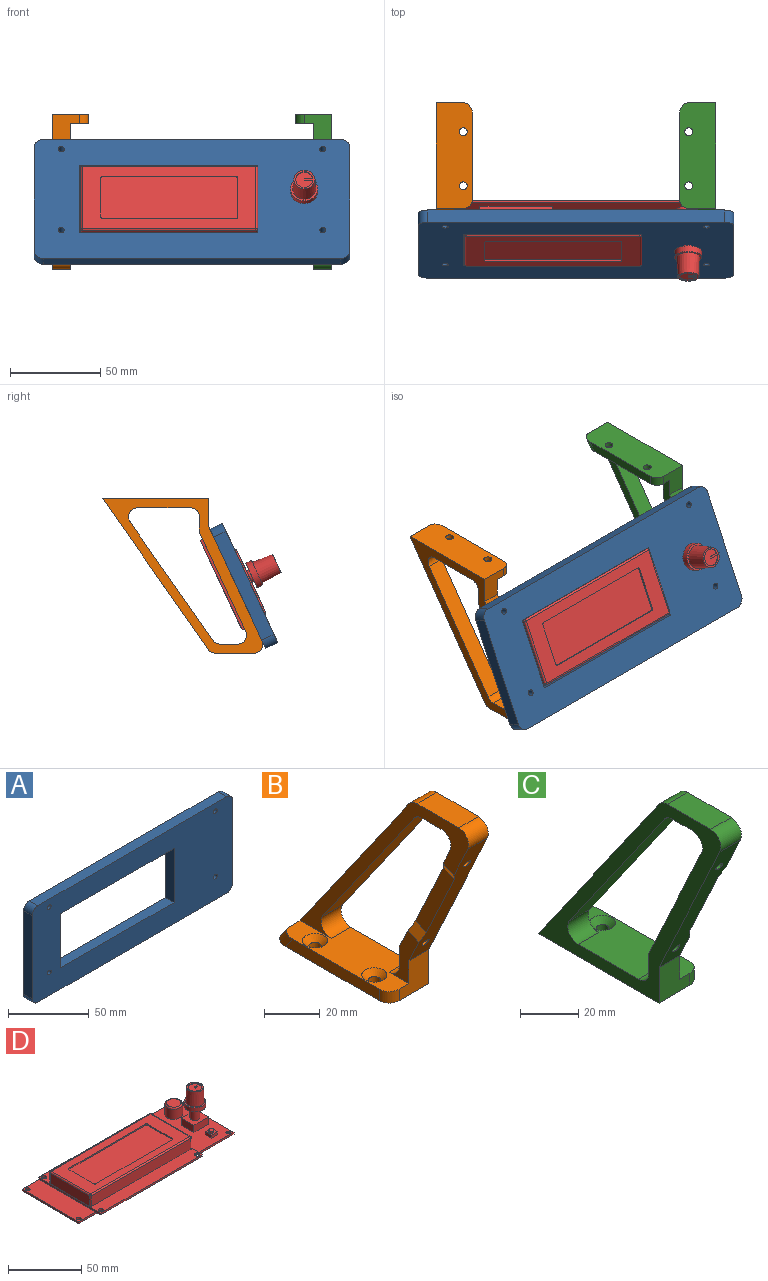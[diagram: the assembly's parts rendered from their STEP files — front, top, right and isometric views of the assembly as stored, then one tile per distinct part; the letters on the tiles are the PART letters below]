
ASSEMBLY  parts=4 mates=3
PART A: 18 faces, bbox 175x7.5x73 mm
  f0: plane 63x7.5mm, normal (1,0,0), area 472.5mm2, adj f8,f9,f10,f13
  f1: plane 165x7.5mm, normal (0,0,1), area 1237.5mm2, adj f8,f9,f10,f11
  f2: plane 63x7.5mm, normal (-1,0,0), area 472.5mm2, adj f8,f9,f11,f12
  f3: plane 99x7.5mm, normal (0,0,1), area 742.5mm2, adj f4,f6,f8,f9
  f4: plane 41x7.5mm, normal (1,0,0), area 307.5mm2, adj f3,f5,f8,f9
  f5: plane 99x7.5mm, normal (0,0,-1), area 742.5mm2, adj f4,f6,f8,f9
  f6: plane 41x7.5mm, normal (-1,0,0), area 307.5mm2, adj f3,f5,f8,f9
  f7: plane 165x7.5mm, normal (0,0,-1), area 1237.5mm2, adj f8,f9,f12,f13
  f8: plane 175x73mm, normal (0,-1,0), area 8660.3mm2, adj f0,f1,f2,f3,f4,f5,f6,f7
  f9: plane 175x73mm, normal (0,1,0), area 8660.3mm2, adj f0,f1,f2,f3,f4,f5,f6,f7
  f10: cylinder r=5mm len=7.5mm, axis (0,1,0), area 58.9mm2, adj f0,f1,f8,f9
  f11: cylinder r=5mm len=7.5mm, axis (0,-1,0), area 58.9mm2, adj f1,f2,f8,f9
  f12: cylinder r=5mm len=7.5mm, axis (0,1,0), area 58.9mm2, adj f2,f7,f8,f9
  f13: cylinder r=5mm len=7.5mm, axis (0,-1,0), area 58.9mm2, adj f0,f7,f8,f9
  f14: cylinder r=1.65mm len=7.5mm, axis (0,1,0), area 77.8mm2, adj f8,f9
  f15: cylinder r=1.65mm len=7.5mm, axis (0,1,0), area 77.8mm2, adj f8,f9
  f16: cylinder r=1.65mm len=7.5mm, axis (0,1,0), area 77.8mm2, adj f8,f9
  f17: cylinder r=1.65mm len=7.5mm, axis (0,1,0), area 77.8mm2, adj f8,f9
PART B: 31 faces, bbox 20x88.7x88.6 mm
  f0: plane 23.15x14.95mm, normal (-1,0,0), area 131.2mm2, adj f1,f4,f5,f9,f10,f22,f24
  f1: plane 55.1x25.7mm, normal (0,0.91,0.42), area 515.3mm2, adj f0,f5,f11,f12,f17,f18,f23,f24
  f2: plane 10x9.55mm, normal (0,0,-1), area 95.5mm2, adj f11,f12,f20,f23
  f3: plane 65.69x46mm, normal (0,-0.82,-0.57), area 802mm2, adj f11,f12,f20,f21
  f4: plane 55.09x20mm, normal (0,0,1), area 706.7mm2, adj f0,f7,f10,f11,f12,f13,f14,f15
  f5: plane 10x8.47mm, normal (0,1,0), area 84.7mm2, adj f0,f1,f11,f22
  f6: plane 58.59x20mm, normal (0,0,-1), area 1129.5mm2, adj f7,f10,f11,f13,f14,f15,f27,f29
  f7: plane 83.56x58.51mm, normal (0,0.82,0.57), area 1050.6mm2, adj f4,f6,f11,f12,f14,f16
  f8: plane 21.1x10mm, normal (0,0,1), area 211mm2, adj f11,f12,f16,f19
  f9: plane 63.58x29.65mm, normal (0,-0.91,-0.42), area 608.8mm2, adj f0,f10,f11,f12,f17,f18,f19,f24
  f10: plane 15x15mm, normal (0,-1,0), area 175mm2, adj f0,f4,f6,f9,f11,f15
  f11: plane 88.71x85.69mm, normal (1,0,0), area 1415.1mm2, adj f1,f2,f3,f4,f5,f6,f7,f8
  f12: plane 85.21x80.69mm, normal (-1,0,0), area 747.2mm2, adj f1,f2,f3,f4,f7,f8,f9,f16
  f13: plane 47.49x5mm, normal (-1,0,0), area 228.7mm2, adj f4,f6,f14,f15
  f14: cylinder r=5mm len=10.74mm, axis (0,0.57,-0.82), area 47.9mm2, adj f4,f6,f7,f13
  f15: cylinder r=5mm len=5mm, axis (0,0,1), area 39.3mm2, adj f4,f6,f10,f13
  f16: cylinder r=5mm len=10mm, axis (-1,0,0), area 48mm2, adj f7,f8,f11,f12
  f17: cylinder r=1.65mm len=6.83mm, axis (0,-0.91,-0.42), area 62.2mm2, adj f1,f9
  f18: cylinder r=1.65mm len=6.83mm, axis (0,-0.91,-0.42), area 62.2mm2, adj f1,f9
  f19: cylinder r=5mm len=10mm, axis (-1,0,0), area 100.4mm2, adj f8,f9,f11,f12
  f20: cylinder r=5mm len=10mm, axis (1,0,0), area 48mm2, adj f2,f3,f11,f12
  f21: cylinder r=5mm len=10mm, axis (1,0,0), area 109.1mm2, adj f3,f4,f11,f12
  f22: cylinder r=5mm len=10mm, axis (1,0,0), area 78.5mm2, adj f0,f4,f5,f11
  f23: cylinder r=5mm len=10mm, axis (1,0,0), area 100.4mm2, adj f1,f2,f11,f12
  f24: plane 7.25x6.42mm, normal (-0.91,-0.18,0.38), area 28.4mm2, adj f0,f1,f9,f25
  f25: plane 32.9x19.6mm, normal (-1,0,0), area 201mm2, adj f1,f9,f24,f26
  f26: plane 7.25x6.42mm, normal (-0.91,0.18,-0.38), area 28.4mm2, adj f1,f9,f12,f25
  f27: cylinder r=2.2mm len=4.4mm, axis (0,0,1), area 37.6mm2, adj f6,f28
  f28: cone r=2.2mm half-angle=45deg, axis (0,0,1), area 67.7mm2, adj f4,f27
  f29: cylinder r=2.2mm len=4.4mm, axis (0,0,1), area 37.6mm2, adj f6,f30
  f30: cone r=2.2mm half-angle=45deg, axis (0,0,1), area 67.7mm2, adj f4,f29
PART C: 31 faces, bbox 20x88.7x88.6 mm
  f0: plane 23.15x14.95mm, normal (1,0,0), area 131.2mm2, adj f1,f4,f5,f9,f10,f22,f24
  f1: plane 55.1x25.7mm, normal (0,0.91,0.42), area 515.3mm2, adj f0,f5,f11,f12,f17,f18,f23,f24
  f2: plane 10x9.55mm, normal (0,0,-1), area 95.5mm2, adj f11,f12,f20,f23
  f3: plane 65.69x46mm, normal (0,-0.82,-0.57), area 802mm2, adj f11,f12,f20,f21
  f4: plane 55.09x20mm, normal (0,0,1), area 706.7mm2, adj f0,f7,f10,f11,f12,f13,f14,f15
  f5: plane 10x8.47mm, normal (0,1,0), area 84.7mm2, adj f0,f1,f11,f22
  f6: plane 58.59x20mm, normal (0,0,-1), area 1129.5mm2, adj f7,f10,f11,f13,f14,f15,f27,f29
  f7: plane 83.56x58.51mm, normal (0,0.82,0.57), area 1050.6mm2, adj f4,f6,f11,f12,f14,f16
  f8: plane 21.1x10mm, normal (0,0,1), area 211mm2, adj f11,f12,f16,f19
  f9: plane 63.58x29.65mm, normal (0,-0.91,-0.42), area 608.8mm2, adj f0,f10,f11,f12,f17,f18,f19,f24
  f10: plane 15x15mm, normal (0,-1,0), area 175mm2, adj f0,f4,f6,f9,f11,f15
  f11: plane 88.71x85.69mm, normal (-1,0,0), area 1415.1mm2, adj f1,f2,f3,f4,f5,f6,f7,f8
  f12: plane 85.21x80.69mm, normal (1,0,0), area 747.2mm2, adj f1,f2,f3,f4,f7,f8,f9,f16
  f13: plane 47.49x5mm, normal (1,0,0), area 228.7mm2, adj f4,f6,f14,f15
  f14: cylinder r=5mm len=10.74mm, axis (0,0.57,-0.82), area 47.9mm2, adj f4,f6,f7,f13
  f15: cylinder r=5mm len=5mm, axis (0,0,1), area 39.3mm2, adj f4,f6,f10,f13
  f16: cylinder r=5mm len=10mm, axis (1,0,0), area 48mm2, adj f7,f8,f11,f12
  f17: cylinder r=1.65mm len=6.83mm, axis (0,-0.91,-0.42), area 62.2mm2, adj f1,f9
  f18: cylinder r=1.65mm len=6.83mm, axis (0,-0.91,-0.42), area 62.2mm2, adj f1,f9
  f19: cylinder r=5mm len=10mm, axis (1,0,0), area 100.4mm2, adj f8,f9,f11,f12
  f20: cylinder r=5mm len=10mm, axis (-1,0,0), area 48mm2, adj f2,f3,f11,f12
  f21: cylinder r=5mm len=10mm, axis (-1,0,0), area 109.1mm2, adj f3,f4,f11,f12
  f22: cylinder r=5mm len=10mm, axis (-1,0,0), area 78.5mm2, adj f0,f4,f5,f11
  f23: cylinder r=5mm len=10mm, axis (-1,0,0), area 100.4mm2, adj f1,f2,f11,f12
  f24: plane 7.25x6.42mm, normal (0.91,-0.18,0.38), area 28.4mm2, adj f0,f1,f9,f25
  f25: plane 32.9x19.6mm, normal (1,0,0), area 201mm2, adj f1,f9,f24,f26
  f26: plane 7.25x6.42mm, normal (0.91,0.18,-0.38), area 28.4mm2, adj f1,f9,f12,f25
  f27: cylinder r=2.2mm len=4.4mm, axis (0,0,1), area 37.6mm2, adj f6,f28
  f28: cone r=2.2mm half-angle=45deg, axis (0,0,1), area 67.7mm2, adj f4,f27
  f29: cylinder r=2.2mm len=4.4mm, axis (0,0,1), area 37.6mm2, adj f6,f30
  f30: cone r=2.2mm half-angle=45deg, axis (0,0,1), area 67.7mm2, adj f4,f29
PART D: 80 faces, bbox 150x62.8x33 mm
  f0: cylinder r=1.75mm len=3.5mm, axis (0,0,-1), area 16.5mm2, adj f14,f79
  f1: cylinder r=7.5mm len=15mm, axis (0,0,-1), area 164.9mm2, adj f18,f66
  f2: cylinder r=3.4mm len=10mm, axis (0,0,-1), area 213.6mm2, adj f19,f66
  f3: torus R=5mm, axis (0,0,1), area 55.6mm2, adj f4,f61
  f4: cylinder r=6mm len=12mm, axis (0,0,-1), area 320.4mm2, adj f3,f15
  f5: cylinder r=1.85mm len=3.7mm, axis (0,0,1), area 17.4mm2, adj f20,f30
  f6: cylinder r=1.85mm len=3.7mm, axis (0,0,1), area 17.4mm2, adj f20,f30
  f7: cylinder r=1.85mm len=3.7mm, axis (0,0,1), area 17.4mm2, adj f20,f30
  f8: cylinder r=1.85mm len=3.7mm, axis (0,0,1), area 17.4mm2, adj f20,f30
  f9: cylinder r=1.6mm len=3.2mm, axis (0,0,1), area 15.1mm2, adj f15,f25
  f10: cylinder r=1.6mm len=3.2mm, axis (0,0,1), area 15.1mm2, adj f15,f25
  f11: cylinder r=1.6mm len=3.2mm, axis (0,0,1), area 15.1mm2, adj f15,f25
  f12: cylinder r=1.6mm len=3.2mm, axis (0,0,1), area 15.1mm2, adj f15,f25
  f13: cone r=6.38mm half-angle=3deg, axis (0,0,-1), area 452.7mm2, adj f18,f67,f68,f69,f73,f74
  f14: plane 6x6mm, normal (0,0,1), area 26.4mm2, adj f0,f75,f76,f77,f78
  f15: plane 150x55mm, normal (0,0,1), area 7780.7mm2, adj f4,f9,f10,f11,f12,f21,f22,f23
  f16: cylinder r=4.75mm len=9.49mm, axis (0,0,1), area 14.4mm2, adj f17,f67,f70,f71
  f17: plane 9.49x9.47mm, normal (0,0,1), area 66mm2, adj f16,f70,f71,f72
  f18: plane 15x15mm, normal (0,0,1), area 49mm2, adj f1,f13
  f19: plane 14x12mm, normal (0,0,1), area 131.7mm2, adj f2,f62,f63,f64,f65
  f20: plane 98.25x60mm, normal (0,0,1), area 1930.9mm2, adj f5,f6,f7,f8,f31,f32,f33,f34
  f21: plane 55x1.5mm, normal (1,0,0), area 82.5mm2, adj f15,f22,f24,f25
  f22: plane 150x1.5mm, normal (0,1,0), area 225mm2, adj f15,f21,f23,f25
  f23: plane 55x1.5mm, normal (-1,0,0), area 82.5mm2, adj f15,f22,f24,f25
  f24: plane 150x1.5mm, normal (0,-1,0), area 225mm2, adj f15,f21,f23,f25
  f25: plane 150x55mm, normal (0,0,-1), area 8217.8mm2, adj f9,f10,f11,f12,f21,f22,f23,f24
  f26: plane 3x3mm, normal (-1,0,0), area 9mm2, adj f15,f27,f29,f30
  f27: plane 40x3mm, normal (0,-1,0), area 120mm2, adj f15,f26,f28,f30
  f28: plane 3x3mm, normal (1,0,0), area 9mm2, adj f15,f27,f29,f30
  f29: plane 40x3mm, normal (0,1,0), area 120mm2, adj f15,f26,f28,f30
  f30: plane 98.25x60mm, normal (0,0,-1), area 5732mm2, adj f5,f6,f7,f8,f26,f27,f28,f29
  f31: plane 60x1.5mm, normal (-1,0,0), area 90mm2, adj f20,f30,f32,f34
  f32: plane 98.25x1.5mm, normal (0,-1,0), area 147.4mm2, adj f20,f30,f31,f33
  f33: plane 60x1.5mm, normal (1,0,0), area 90mm2, adj f20,f30,f32,f34
  f34: plane 98.25x1.5mm, normal (0,1,0), area 147.4mm2, adj f20,f30,f31,f33
  f35: plane 38x9mm, normal (-1,0,0), area 342mm2, adj f20,f42,f47,f48
  f36: plane 96.05x9mm, normal (0,-1,0), area 864.4mm2, adj f20,f40,f41,f42
  f37: plane 38x9mm, normal (1,0,0), area 342mm2, adj f20,f40,f45,f46
  f38: plane 96.05x9mm, normal (0,1,0), area 864.4mm2, adj f20,f45,f48,f51
  f39: plane 96.05x38mm, normal (0,0,1), area 1674.8mm2, adj f41,f46,f47,f51,f52,f53,f54,f55
  f40: cylinder r=1mm len=9mm, axis (0,0,-1), area 14.1mm2, adj f20,f36,f37,f43
  f41: cylinder r=1mm len=96.05mm, axis (-1,0,0), area 150.9mm2, adj f36,f39,f43,f44
  f42: cylinder r=1mm len=9mm, axis (0,0,-1), area 14.1mm2, adj f20,f35,f36,f44
  f43: sphere r=1mm, area 1.6mm2, adj f40,f41,f46
  f44: sphere r=1mm, area 1.6mm2, adj f41,f42,f47
  f45: cylinder r=1mm len=9mm, axis (0,0,-1), area 14.1mm2, adj f20,f37,f38,f49
  f46: cylinder r=1mm len=38mm, axis (0,-1,0), area 59.7mm2, adj f37,f39,f43,f49
  f47: cylinder r=1mm len=38mm, axis (0,1,0), area 59.7mm2, adj f35,f39,f44,f50
  f48: cylinder r=1mm len=9mm, axis (0,0,-1), area 14.1mm2, adj f20,f35,f38,f50
  f49: sphere r=1mm, area 1.6mm2, adj f45,f46,f51
  f50: sphere r=1mm, area 1.6mm2, adj f47,f48,f51
  f51: cylinder r=1mm len=96.05mm, axis (1,0,0), area 150.9mm2, adj f38,f39,f49,f50
  f52: plane 24x1mm, normal (-1,0,0), area 24mm2, adj f39,f56,f57,f60
  f53: plane 74x1mm, normal (0,1,0), area 74mm2, adj f39,f56,f59,f60
  f54: plane 24x1mm, normal (1,0,0), area 24mm2, adj f39,f56,f58,f59
  f55: plane 74x1mm, normal (0,-1,0), area 74mm2, adj f39,f56,f57,f58
  f56: plane 76x26mm, normal (0,0,1), area 1975.1mm2, adj f52,f53,f54,f55,f57,f58,f59,f60
  f57: cylinder r=1mm len=1mm, axis (0,0,-1), area 1.6mm2, adj f39,f52,f55,f56
  f58: cylinder r=1mm len=1mm, axis (0,0,-1), area 1.6mm2, adj f39,f54,f55,f56
  f59: cylinder r=1mm len=1mm, axis (0,0,-1), area 1.6mm2, adj f39,f53,f54,f56
  f60: cylinder r=1mm len=1mm, axis (0,0,-1), area 1.6mm2, adj f39,f52,f53,f56
  f61: plane 10x10mm, normal (0,0,1), area 78.5mm2, adj f3
  f62: plane 12x6mm, normal (1,0,0), area 72mm2, adj f15,f19,f63,f65
  f63: plane 14x6mm, normal (0,1,0), area 84mm2, adj f15,f19,f62,f64
  f64: plane 12x6mm, normal (-1,0,0), area 72mm2, adj f15,f19,f63,f65
  f65: plane 14x6mm, normal (0,-1,0), area 84mm2, adj f15,f19,f62,f64
  f66: plane 15x15mm, normal (0,0,-1), area 140.4mm2, adj f1,f2
  f67: plane 11.99x11.49mm, normal (0,0,1), area 38mm2, adj f13,f16,f68,f69,f70,f71,f72,f73
  f68: plane 0.41x0.02mm, normal (0,-1,0), area 0mm2, adj f13,f67,f73
  f69: plane 0.41x0.02mm, normal (0,1,0), area 0mm2, adj f13,f67,f74
  f70: plane 4.72x0.5mm, normal (0,-1,0), area 2.4mm2, adj f16,f17,f67,f72
  f71: plane 4.72x0.5mm, normal (0,1,0), area 2.4mm2, adj f16,f17,f67,f72
  f72: plane 1x0.5mm, normal (-1,0,0), area 0.5mm2, adj f17,f67,f70,f71
  f73: plane 9.54x0.5mm, normal (0.71,-0.71,0), area 3.5mm2, adj f13,f67,f68,f74
  f74: plane 9.54x0.5mm, normal (0.71,0.71,0), area 3.5mm2, adj f13,f67,f69,f73
  f75: plane 6x2.5mm, normal (1,0,0), area 15mm2, adj f14,f15,f76,f78
  f76: plane 6x2.5mm, normal (0,1,0), area 15mm2, adj f14,f15,f75,f77
  f77: plane 6x2.5mm, normal (-1,0,0), area 15mm2, adj f14,f15,f76,f78
  f78: plane 6x2.5mm, normal (0,-1,0), area 15mm2, adj f14,f15,f75,f77
  f79: plane 3.5x3.5mm, normal (0,0,1), area 9.6mm2, adj f0
PLACE A rot(axis=(-1,0,0),25deg) t=(-69.66,-140.07,47.62)mm
PLACE B rot(axis=(0,-1,0),180deg) t=(-137.16,-123.8,97.51)mm
PLACE C rot(axis=(0,-1,0),180deg) t=(47.84,-123.8,97.51)mm
PLACE D rot(axis=(1,0,0),65deg) t=(-69.91,-130.85,49.66)mm
MATE fastened B.f18 <-> A.f14  axis (0,-0.91,0.42) through (-142.16,-127.18,75.26)mm
MATE fastened C.f18 <-> A.f17  axis (0,-0.91,0.42) through (2.84,-127.18,75.26)mm
MATE fastened D.f11 <-> B.f18  axis (0,-0.91,0.42) through (-142.16,-121.74,72.72)mm
